# Revit family: Hager-Univers-IP44-D205-H500-Cl.I-Encl-NoHosted-CH-fr
name_source: partatom
category: Electrical Equipment
units: mm (PartAtom-declared; Revit-internal decimal feet)

## family parameters
Always vertical = Yes
Cut with Voids When Loaded = No
Panel Configuration = Two Columns, Circuits Across
Part Type = Panelboard
Room Calculation Point = No
Round Connector Dimension = Use Diameter
Shared = No
Work Plane-Based = Yes

## types (10) — shared parameters
Default Elevation = 1219 mm
EF000003 - mode de pose = EV000384 - saillie
EF000007 - couleur = EV000202 - blanc
EF000040 - hauteur = 500 mm  [stored 1.64042 ft]
EF000049 - profondeur = 205 mm  [stored 0.672572 ft]
EF000116 - numéro RAL = 9010
EF000118 - avec cadre/support de montage = No
EF000266 - nombre de rangées = 3
EF000339 - type de capot = EV001012 - couvercle
EF001088 - possibilité de montage en saillie = Yes
EF001131 - profondeur intérieure = 205 mm  [stored 0.672572 ft]
EF001596 - matériau du boîtier/corps = EV000179 - acier
EF001613 - maintien de fonction = EV000494 - sans
EF003532 - convient pour utilisation à l’extérieur = No
EF004293 - indice de protection contre les chocs (IK) = EV006815 - IK09
EF005474 - indice de protection (IP) = EV006418 - IP44
EF006244 - couvercle/porte transparent(e) = No
EF006306 - avec serrure = No
EF007800 - adapté à un parafoudre = No
EF008873 - courant nominal (In) = 250 A
EF009170 - épaisseur de matériau du boîtier = 1 mm  [stored 0.00328084 ft]
EF009171 - épaisseur de matériau de la porte/du couvercle = 1 mm  [stored 0.00328084 ft]
EF009212 - finition du couvercle = EV000116 - fermé
EF015940 - couvercle avec décharge de pression = No
HG000002 - avec porte = Yes
HG000003 - Gamme = Univers
HG000006 - Encastré = No
HG000023 - Armoire double section = No
HG000024 - Hauteur de la section basse = 600 mm
HG000026 - Installation au sol = No
Manufacturer = Hager
Type Comments = Univers
zero-valued in all types: HG000027 - Hauteur du socle

## per-type parameters (varying)
| type | EF000008 - largeur | EF000218 - profondeur d'encastrement | EF000437 - nombre d'entrées de conduit | EF002950 - largeur en nombre de modules | EF004427 - nombre de modules | EF004464 - type de porte | EF009554 - nombre d'ouvertures pour plaques à bride | HG000004 - Référence fabricant | HG000009 - Porte à double battant | HG000010 - Portes asymétriques |
| saillie IP44 L1050 H500 P205  - FP34QT | 1050 mm | 0 mm  [stored 0 ft] | 8 | 48 | 144 | EV003602 - double | 8 | FP34QT | No | No |
| saillie IP44 L1050 H500 P205  - FP34TN2 | 1050 mm | 205 mm  [stored 0.672572 ft] | 8 | 48 | 144 | EV003602 - double | 8 | FP34TN2 | Yes | No |
| saillie IP44 L1300 H500 P205  - FP35QT | 1300 mm  [stored 4.26509 ft] | 0 mm  [stored 0 ft] | 10 | 60 | 180 | EV003602 - double | 10 | FP35QT | No | No |
| saillie IP44 L1300 H500 P205  - FP35TN2 | 1300 mm  [stored 4.26509 ft] | 205 mm  [stored 0.672572 ft] | 10 | 60 | 180 | EV003602 - double | 10 | FP35TN2 | Yes | Yes |
| saillie IP44 L300 H500 P205  - FP31QT | 300 mm | 0 mm  [stored 0 ft] | 2 | 12 | 36 | EV002646 - unique | 2 | FP31QT | No | No |
| saillie IP44 L300 H500 P205  - FP31TN2 | 300 mm | 205 mm  [stored 0.672572 ft] | 2 | 12 | 36 | EV002646 - unique | 2 | FP31TN2 | No | No |
| saillie IP44 L550 H500 P205  - FP32QT | 550 mm | 0 mm  [stored 0 ft] | 4 | 24 | 72 | EV002646 - unique | 4 | FP32QT | No | No |
| saillie IP44 L550 H500 P205  - FP32TN2 | 550 mm | 205 mm  [stored 0.672572 ft] | 4 | 24 | 72 | EV002646 - unique | 4 | FP32TN2 | No | No |
| saillie IP44 L800 H500 P205  - FP33QT | 800 mm  [stored 2.62467 ft] | 0 mm  [stored 0 ft] | 6 | 36 | 108 | EV002646 - unique | 6 | FP33QT | No | No |
| saillie IP44 L800 H500 P205  - FP33TN2 | 800 mm  [stored 2.62467 ft] | 205 mm  [stored 0.672572 ft] | 6 | 36 | 108 | EV002646 - unique | 6 | FP33TN2 | No | No |

note: [stored X ft] marks values corroborated as IEEE doubles in the binary element streams (Revit-internal decimal feet)

## geometry (parser evidence)
native form markers: Blend x4, Sweep x11
no freeform markers — native parametric forms only
